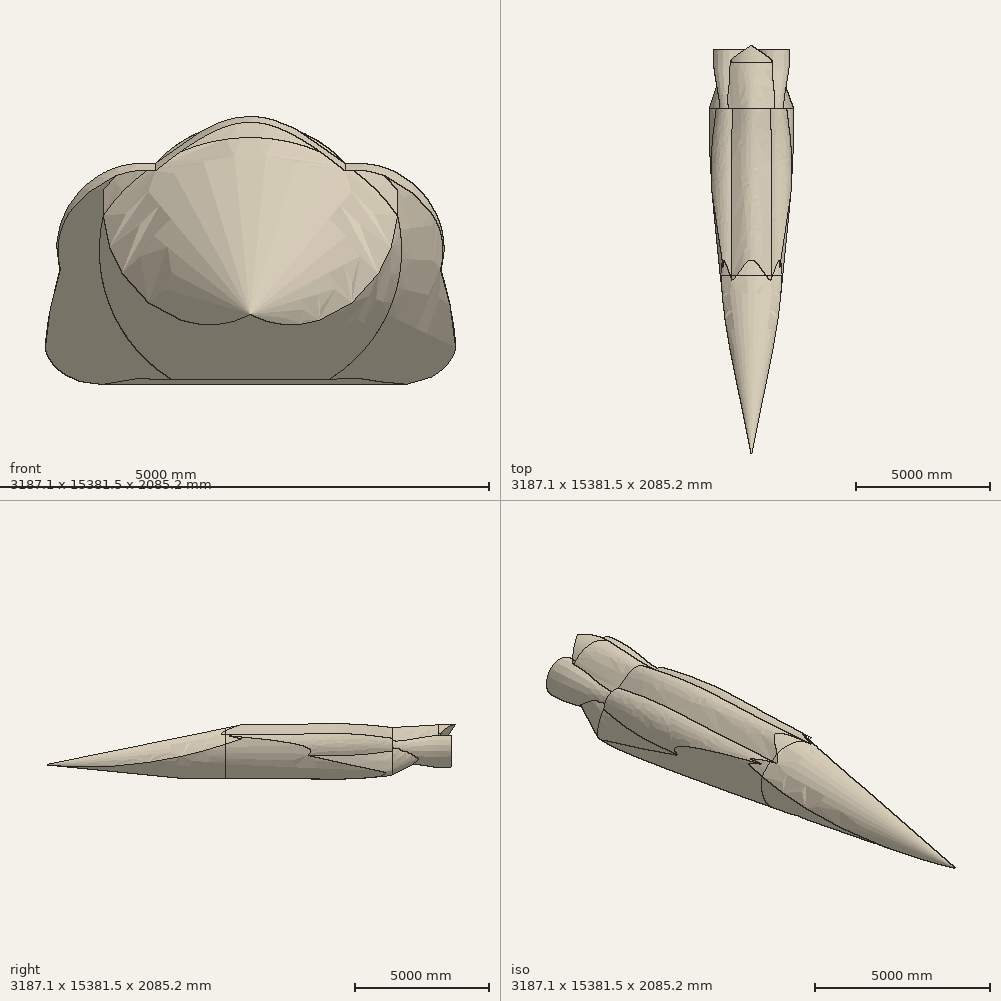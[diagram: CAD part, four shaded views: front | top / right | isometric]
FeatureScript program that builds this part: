
annotation { "Feature Type Name" : "Feature", "Feature Type Description" : "" }
export const myFeature = defineFeature(function(context is Context, id is Id, definition is map)
    precondition{}
    {
        {
            var Q0;
            Q0=qCreatedBy(makeId("Front.planeOp"),FACE);
            cPlane(context, id + "F0", {"entities" : qUnion([Q0]), "cplaneType" : CPlaneType.OFFSET, "offset" : 1750 * mm, "width" : 152.4 * mm, "height" : 152.4 * mm});
        }
        {
            var Q0;
            Q0=qCreatedBy(id+"F0.planeOp",FACE);
            var sketch = newSketch(context, id + "F1", { "sketchPlane" : qUnion([Q0])});
            skLineSegment(sketch, "E0.top", {"start": v(-1394.2, -1000) * mm, "end": v(1394.2, -1000) * mm});
            skPoint(sketch, "E0.middle", {"position": v(0, 0) * mm});
            skFitSpline(sketch, "E1", {"points": [v(-1600, -1000) * mm, v(-848, 530) * mm, v(0, 1000) * mm, v(848, 530) * mm, v(1600, -1000) * mm], "startDerivative": vector(0, 10524.75) * mm, "endDerivative": vector(0, -10524.75) * mm});
            skArc(sketch, "E2", {"start": v(-735.27, 618.52) * mm, "mid": v(-1273.27, 435.52) * mm, "end": v(-1440.68, -107.53) * mm});
            skArc(sketch, "E3.trimOffspring", {"start": v(1440.68, -107.53) * mm, "mid": v(1273.27, 435.52) * mm, "end": v(735.27, 618.52) * mm});
            skFitSpline(sketch, "E4.trimOffspring", {"points": [v(-1600, -1000) * mm, v(-848, 530) * mm, v(0, 1000) * mm, v(848, 530) * mm, v(1600, -1000) * mm], "startDerivative": vector(0, 10524.75) * mm, "endDerivative": vector(0, -10524.75) * mm});
            skFitSpline(sketch, "E5.trimOffspring", {"points": [v(-1600, -1000) * mm, v(-848, 530) * mm, v(0, 1000) * mm, v(848, 530) * mm, v(1600, -1000) * mm], "startDerivative": vector(0, 10524.75) * mm, "endDerivative": vector(0, -10524.75) * mm});
            skArc(sketch, "E6.filletArc", {"start": v(-1593.82, -787.83) * mm, "mid": v(-1539.85, -937.05) * mm, "end": v(-1394.2, -1000) * mm});
            skArc(sketch, "E7.filletArc", {"start": v(1394.2, -1000) * mm, "mid": v(1539.85, -937.05) * mm, "end": v(1593.82, -787.83) * mm});
            skSolve(sketch);
        }
        {
            var Q0;
            Q0=qCreatedBy(makeId("Front.planeOp"),FACE);
            var sketch = newSketch(context, id + "F2", { "sketchPlane" : qUnion([Q0])});
            skLineSegment(sketch, "E8.top", {"start": v(-1394.2, -1000) * mm, "end": v(1394.2, -1000) * mm});
            skPoint(sketch, "E8.middle", {"position": v(0, 0) * mm});
            skFitSpline(sketch, "E9", {"points": [v(-1600, -1000) * mm, v(-848, 530) * mm, v(0, 1000) * mm, v(848, 530) * mm, v(1600, -1000) * mm], "startDerivative": vector(0, 10524.75) * mm, "endDerivative": vector(0, -10524.75) * mm});
            skArc(sketch, "E10", {"start": v(-735.27, 618.52) * mm, "mid": v(-1273.27, 435.52) * mm, "end": v(-1440.68, -107.53) * mm});
            skArc(sketch, "E11.trimOffspring", {"start": v(1440.68, -107.53) * mm, "mid": v(1273.27, 435.52) * mm, "end": v(735.27, 618.52) * mm});
            skFitSpline(sketch, "E12.trimOffspring", {"points": [v(-1600, -1000) * mm, v(-848, 530) * mm, v(0, 1000) * mm, v(848, 530) * mm, v(1600, -1000) * mm], "startDerivative": vector(0, 10524.75) * mm, "endDerivative": vector(0, -10524.75) * mm});
            skFitSpline(sketch, "E13.trimOffspring", {"points": [v(-1600, -1000) * mm, v(-848, 530) * mm, v(0, 1000) * mm, v(848, 530) * mm, v(1600, -1000) * mm], "startDerivative": vector(0, 10524.75) * mm, "endDerivative": vector(0, -10524.75) * mm});
            skArc(sketch, "E14.filletArc", {"start": v(-1593.82, -787.83) * mm, "mid": v(-1539.85, -937.05) * mm, "end": v(-1394.2, -1000) * mm});
            skArc(sketch, "E15.filletArc", {"start": v(1394.2, -1000) * mm, "mid": v(1539.85, -937.05) * mm, "end": v(1593.82, -787.83) * mm});
            skSolve(sketch);
        }
        {
            var Q0;
            Q0=qCreatedBy(makeId("Front.planeOp"),FACE);
            cPlane(context, id + "F3", {"entities" : qUnion([Q0]), "cplaneType" : CPlaneType.OFFSET, "offset" : 3500 * mm, "oppositeDirection" : true, "width" : 150 * mm, "height" : 150 * mm});
        }
        {
            var Q0;
            Q0=qCreatedBy(id+"F3.planeOp",FACE);
            var sketch = newSketch(context, id + "F4", { "sketchPlane" : qUnion([Q0])});
            skLineSegment(sketch, "E16.top", {"start": v(-1394.2, -1000) * mm, "end": v(1394.2, -1000) * mm});
            skPoint(sketch, "E16.middle", {"position": v(0, 0) * mm});
            skFitSpline(sketch, "E17", {"points": [v(-1600, -1000) * mm, v(-848, 530) * mm, v(0, 1000) * mm, v(848, 530) * mm, v(1600, -1000) * mm], "startDerivative": vector(0, 10524.75) * mm, "endDerivative": vector(0, -10524.75) * mm});
            skArc(sketch, "E18", {"start": v(-735.27, 618.52) * mm, "mid": v(-1273.27, 435.52) * mm, "end": v(-1440.68, -107.53) * mm});
            skArc(sketch, "E19.trimOffspring", {"start": v(1440.68, -107.53) * mm, "mid": v(1273.27, 435.52) * mm, "end": v(735.27, 618.52) * mm});
            skFitSpline(sketch, "E20.trimOffspring", {"points": [v(-1600, -1000) * mm, v(-848, 530) * mm, v(0, 1000) * mm, v(848, 530) * mm, v(1600, -1000) * mm], "startDerivative": vector(0, 10524.75) * mm, "endDerivative": vector(0, -10524.75) * mm});
            skFitSpline(sketch, "E21.trimOffspring", {"points": [v(-1600, -1000) * mm, v(-848, 530) * mm, v(0, 1000) * mm, v(848, 530) * mm, v(1600, -1000) * mm], "startDerivative": vector(0, 10524.75) * mm, "endDerivative": vector(0, -10524.75) * mm});
            skArc(sketch, "E22.filletArc", {"start": v(-1593.82, -787.83) * mm, "mid": v(-1539.85, -937.05) * mm, "end": v(-1394.2, -1000) * mm});
            skArc(sketch, "E23.filletArc", {"start": v(1394.2, -1000) * mm, "mid": v(1539.85, -937.05) * mm, "end": v(1593.82, -787.83) * mm});
            skSolve(sketch);
        }
        {
            var Q0;
            Q0=qCreatedBy(makeId("Front.planeOp"),FACE);
            cPlane(context, id + "F5", {"entities" : qUnion([Q0]), "cplaneType" : CPlaneType.OFFSET, "offset" : 4500 * mm, "oppositeDirection" : true, "width" : 150 * mm, "height" : 150 * mm});
        }
        {
            var Q0;
            Q0=qCreatedBy(id+"F5.planeOp",FACE);
            var sketch = newSketch(context, id + "F6", { "sketchPlane" : qUnion([Q0])});
            skLineSegment(sketch, "E24.top", {"start": v(-1413.07, -900) * mm, "end": v(1413.07, -900) * mm});
            skPoint(sketch, "E24.middle", {"position": v(0, 0) * mm});
            skFitSpline(sketch, "E25", {"points": [v(-1600, -900) * mm, v(-784.42, 441.24) * mm, v(0, 900) * mm, v(784.42, 441.24) * mm, v(1600, -900) * mm], "startDerivative": vector(0, 9508.62) * mm, "endDerivative": vector(0, -9508.62) * mm});
            skArc(sketch, "E26", {"start": v(-719.25, 488.69) * mm, "mid": v(-1131.76, 394.84) * mm, "end": v(-1324.66, 18.33) * mm});
            skArc(sketch, "E27.trimOffspring", {"start": v(1324.66, 18.33) * mm, "mid": v(1131.76, 394.84) * mm, "end": v(719.25, 488.69) * mm});
            skFitSpline(sketch, "E28.trimOffspring", {"points": [v(-1600, -900) * mm, v(-784.42, 441.24) * mm, v(0, 900) * mm, v(784.42, 441.24) * mm, v(1600, -900) * mm], "startDerivative": vector(0, 9508.62) * mm, "endDerivative": vector(0, -9508.62) * mm});
            skFitSpline(sketch, "E29.trimOffspring", {"points": [v(-1600, -900) * mm, v(-784.42, 441.24) * mm, v(0, 900) * mm, v(784.42, 441.24) * mm, v(1600, -900) * mm], "startDerivative": vector(0, 9508.62) * mm, "endDerivative": vector(0, -9508.62) * mm});
            skArc(sketch, "E30.filletArc", {"start": v(-1592.48, -705.43) * mm, "mid": v(-1545.4, -842.02) * mm, "end": v(-1413.07, -900) * mm});
            skArc(sketch, "E31.filletArc", {"start": v(1413.07, -900) * mm, "mid": v(1545.4, -842.02) * mm, "end": v(1592.48, -705.43) * mm});
            skLineSegment(sketch, "E32", {"start": v(-719.25, 488.69) * mm, "end": v(-1324.66, 18.33) * mm, "construction": true});
            skLineSegment(sketch, "E33", {"start": v(719.25, 488.69) * mm, "end": v(1324.66, 18.33) * mm, "construction": true});
            skSolve(sketch);
        }
        {
            var Q0;
            Q0=qCreatedBy(makeId("Front.planeOp"),FACE);
            cPlane(context, id + "F7", {"entities" : qUnion([Q0]), "cplaneType" : CPlaneType.OFFSET, "offset" : 6232.05 * mm, "oppositeDirection" : true, "width" : 150 * mm, "height" : 150 * mm});
        }
        {
            var Q0;
            Q0=qCreatedBy(id+"F7.planeOp",FACE);
            var sketch = newSketch(context, id + "F8", { "sketchPlane" : qUnion([Q0])});
            skArc(sketch, "E34", {"start": v(998.61, 52.63) * mm, "mid": v(0, 1000) * mm, "end": v(-998.61, 52.63) * mm});
            skLineSegment(sketch, "E35", {"start": v(0, 0) * mm, "end": v(-948.68, 0) * mm});
            skLineSegment(sketch, "E36", {"start": v(0, 0) * mm, "end": v(948.68, 0) * mm});
            skPoint(sketch, "E37.visualSharp", {"position": v(-1000, 0) * mm});
            skArc(sketch, "E37.filletArc", {"start": v(-998.61, 52.63) * mm, "mid": v(-984.96, 15.59) * mm, "end": v(-948.68, 0) * mm});
            skPoint(sketch, "E38.visualSharp", {"position": v(1000, 0) * mm});
            skArc(sketch, "E38.filletArc", {"start": v(948.68, 0) * mm, "mid": v(984.96, 15.59) * mm, "end": v(998.61, 52.63) * mm});
            skLineSegment(sketch, "E39", {"start": v(0, 1000) * mm, "end": v(0, 675) * mm, "construction": true});
            skPoint(sketch, "E39.endSnap0", {"position": v(0, 1000) * mm});
            skLineSegment(sketch, "E40", {"start": v(0, 675) * mm, "end": v(737.82, 675) * mm, "construction": true});
            skLineSegment(sketch, "E41", {"start": v(0, 675) * mm, "end": v(-737.82, 675) * mm, "construction": true});
            skSolve(sketch);
        }
        {
            var Q0;
            Q0 = qSketchRegion(id + "F1", true);
            var Q1;
            Q1 = qSketchRegion(id + "F2", true);
            var Q2;
            Q2 = qSketchRegion(id + "F4", true);
            var Q3;
            Q3 = qSketchRegion(id + "F6", true);
            loft(context, id + "F9", {"sheetProfilesArray" : [{ "sheetProfileEntities" : qUnion([Q0]) }, { "sheetProfileEntities" : qUnion([Q1]) }, { "sheetProfileEntities" : qUnion([Q2]) }, { "sheetProfileEntities" : qUnion([Q3]) }]});
        }
        {
            var Q0;
            Q0=sQuery(id+"F6.wireOp",EDGE,"E32");
            var Q1;
            Q1=sQuery(id+"F8.wireOp",VERTEX,"E41.end");
            cPlane(context, id + "F10", {"entities" : qUnion([Q0, Q1]), "cplaneType" : CPlaneType.LINE_ANGLE, "offset" : 25 * mm, "angle" : 0 * degree, "width" : 150 * mm, "height" : 150 * mm});
        }
        {
            var Q0;
            Q0=qCreatedBy(id+"F10.planeOp",FACE);
            var sketch = newSketch(context, id + "F11", { "sketchPlane" : qUnion([Q0])});
            skLineSegment(sketch, "E42", {"start": v(-589.34, -4526.34) * mm, "end": v(-612.8, -6268.32) * mm});
            skLineSegment(sketch, "E43", {"start": v(-1354.08, -4472.19) * mm, "end": v(-612.8, -6268.32) * mm});
            skSolve(sketch);
        }
        {
            var Q0;
            Q0=sQuery(id+"F6.wireOp",EDGE,"E33");
            var Q1;
            Q1=sQuery(id+"F8.wireOp",VERTEX,"E40.end");
            cPlane(context, id + "F12", {"entities" : qUnion([Q0, Q1]), "cplaneType" : CPlaneType.LINE_ANGLE, "offset" : 25 * mm, "angle" : 0 * degree, "width" : 150 * mm, "height" : 150 * mm});
        }
        {
            var Q0;
            Q0=qCreatedBy(id+"F12.planeOp",FACE);
            var sketch = newSketch(context, id + "F13", { "sketchPlane" : qUnion([Q0])});
            skLineSegment(sketch, "E44", {"start": v(589.34, 4526.34) * mm, "end": v(612.8, 6268.32) * mm});
            skLineSegment(sketch, "E45", {"start": v(1354.08, 4472.19) * mm, "end": v(612.8, 6268.32) * mm});
            skSolve(sketch);
        }
        {
            var Q1;
            Q1=makeQuery(id+"F6.imprint","IMPRINT",FACE,{"disambiguationData":[TD([[makeQuery(id+"F6.imprint","IMPRINT",EDGE,{"derivedFrom":sQuery(id+"F6.wireOp",EDGE,"E24.top")}),1.0]])]});
            var Q2;
            Q2=makeQuery(id+"F8.imprint","IMPRINT",FACE,{"disambiguationData":[TD([[makeQuery(id+"F8.imprint","IMPRINT",EDGE,{"derivedFrom":sQuery(id+"F8.wireOp",EDGE,"E34")}),1.0]])]});
            var Q3;
            Q3=sQuery(id+"F11.wireOp",EDGE,"E42");
            var Q4;
            Q4=sQuery(id+"F13.wireOp",EDGE,"E44");
            loft(context, id + "F14", {"operationType" : NewBodyOperationType.ADD, "addGuides" : true, "sheetProfilesArray" : [{ "sheetProfileEntities" : qUnion([Q1]) }, { "sheetProfileEntities" : qUnion([Q2]) }], "guidesArray" : [{ "guideEntities" : qUnion([Q3]), "guideDerivativeType" : LoftGuideDerivativeType.DEFAULT, "guideDerivativeMagnitude" : 1 }, { "guideEntities" : qUnion([Q4]), "guideDerivativeType" : LoftGuideDerivativeType.DEFAULT, "guideDerivativeMagnitude" : 1 }]});
        }
        {
            var Q0;
            Q0=makeQuery(id+"F14.opLoft","CAP_FACE",FACE,{"disambiguationData":[OSD([makeQuery(id+"F8.imprint","IMPRINT",FACE,{"disambiguationData":[TD([[makeQuery(id+"F8.imprint","IMPRINT",EDGE,{"derivedFrom":sQuery(id+"F8.wireOp",EDGE,"E34")}),1.0]])]})])],"isStart":true});
            extrude(context, id + "F15", {"entities" : qUnion([Q0]), "operationType" : NewBodyOperationType.ADD, "depth" : 649.4 * mm});
        }
        {
            var Q0;
            Q0=qCreatedBy(makeId("Right.planeOp"),FACE);
            var sketch = newSketch(context, id + "F16", { "sketchPlane" : qUnion([Q0])});
            skLineSegment(sketch, "E46", {"start": v(0, 0) * mm, "end": v(4500, 0) * mm});
            skLineSegment(sketch, "E47", {"start": v(4500, 0) * mm, "end": v(6232.05, 0) * mm});
            skLineSegment(sketch, "E48", {"start": v(4500, 0) * mm, "end": v(4500, 1000) * mm});
            skLineSegment(sketch, "E49", {"start": v(4500, 1000) * mm, "end": v(6881.46, 1000) * mm});
            skLineSegment(sketch, "E50", {"start": v(6881.46, 1000) * mm, "end": v(6881.46, -1000) * mm});
            skLineSegment(sketch, "E51", {"start": v(6881.46, 1000) * mm, "end": v(6232.05, 0) * mm});
            skLineSegment(sketch, "E52", {"start": v(6232.05, 0) * mm, "end": v(5582.64, -1000) * mm});
            skLineSegment(sketch, "E53", {"start": v(5582.64, -1000) * mm, "end": v(6881.46, -1000) * mm});
            skSolve(sketch);
        }
        {
            var Q0;
            Q0=makeQuery(id+"F16.imprint","IMPRINT",FACE,{"disambiguationData":[TD([[makeQuery(id+"F16.imprint","IMPRINT",EDGE,{"derivedFrom":sQuery(id+"F16.wireOp",EDGE,"E50")}),-1.0]])]});
            var Q1;
            Q1=sQuery(id+"F16.wireOp",EDGE,"E49");
            revolve(context, id + "F17", {"operationType" : NewBodyOperationType.REMOVE, "entities" : qUnion([Q0]), "axis" : qUnion([Q1]), "revolveType" : RevolveType.SYMMETRIC, "oppositeDirection" : true, "angle" : 182 * degree});
        }
        {
            var Q0;
            Q0=makeQuery(id+"F9.opLoft","CAP_FACE",FACE,{"disambiguationData":[OSD([makeQuery(id+"F1.imprint","IMPRINT",FACE,{"disambiguationData":[TD([[makeQuery(id+"F1.imprint","IMPRINT",EDGE,{"derivedFrom":sQuery(id+"F1.wireOp",EDGE,"E0.top")}),1.0]])]})])],"isStart":true});
            extrude(context, id + "F18", {"entities" : qUnion([Q0]), "depth" : 6750 * mm});
        }
        {
            var Q0;
            Q0=qCreatedBy(makeId("Right.planeOp"),FACE);
            var sketch = newSketch(context, id + "F19", { "sketchPlane" : qUnion([Q0])});
            skLineSegment(sketch, "E54", {"start": v(0, 0) * mm, "end": v(-3500, 0) * mm});
            skLineSegment(sketch, "E55", {"start": v(-3500, 0) * mm, "end": v(-3500, -1000) * mm});
            skLineSegment(sketch, "E56", {"start": v(-3500, -1000) * mm, "end": v(-8500, -1000) * mm});
            skLineSegment(sketch, "E57", {"start": v(-8500, -1000) * mm, "end": v(-8500, -499.31) * mm});
            skLineSegment(sketch, "E58", {"start": v(-1151.4, 0) * mm, "end": v(-1151.4, 1000) * mm});
            skLineSegment(sketch, "E59", {"start": v(-1151.4, 1000) * mm, "end": v(-8500, -499.31) * mm});
            skLineSegment(sketch, "E60", {"start": v(-8500, -499.31) * mm, "end": v(-3500, -1000) * mm});
            skLineSegment(sketch, "E61", {"start": v(-1151.4, 1000) * mm, "end": v(-8500, 1000) * mm});
            skLineSegment(sketch, "E62", {"start": v(-8500, 1000) * mm, "end": v(-8500, -499.31) * mm});
            skLineSegment(sketch, "E63", {"start": v(-8500, -1000) * mm, "end": v(-8500, -1980) * mm});
            skLineSegment(sketch, "E64", {"start": v(-3500, -1000) * mm, "end": v(6286.5, -1980) * mm});
            skLineSegment(sketch, "E65", {"start": v(6286.5, -1980) * mm, "end": v(-8500, -1980) * mm});
            skLineSegment(sketch, "E66", {"start": v(-8500, -499.31) * mm, "end": v(-3500, -499.31) * mm});
            skSolve(sketch);
        }
        {
            var Q0;
            Q0=makeQuery(id+"F19.imprint","IMPRINT",FACE,{"disambiguationData":[TD([[makeQuery(id+"F19.imprint","IMPRINT",EDGE,{"derivedFrom":sQuery(id+"F19.wireOp",EDGE,"E59")}),-1.0]])]});
            var Q1;
            Q1=sQuery(id+"F19.wireOp",EDGE,"E66");
            revolve(context, id + "F20", {"operationType" : NewBodyOperationType.REMOVE, "entities" : qUnion([Q0]), "axis" : qUnion([Q1]), "revolveType" : RevolveType.SYMMETRIC, "oppositeDirection" : true, "angle" : 250 * degree});
        }
        {
            var Q0;
            Q0=makeQuery(id+"F19.imprint","IMPRINT",FACE,{"disambiguationData":[TD([[makeQuery(id+"F19.imprint","IMPRINT",EDGE,{"derivedFrom":sQuery(id+"F19.wireOp",EDGE,"E56")}),-1.0]])]});
            var Q1;
            Q1=makeQuery(id+"F19.imprint","IMPRINT",FACE,{"disambiguationData":[TD([[makeQuery(id+"F19.imprint","IMPRINT",EDGE,{"derivedFrom":sQuery(id+"F19.wireOp",EDGE,"E56")}),1.0]])]});
            var Q2;
            Q2=sQuery(id+"F19.wireOp",EDGE,"E54");
            revolve(context, id + "F21", {"operationType" : NewBodyOperationType.REMOVE, "entities" : qUnion([Q0, Q1]), "axis" : qUnion([Q2]), "revolveType" : RevolveType.SYMMETRIC, "oppositeDirection" : true, "angle" : 240 * degree});
        }
        {
            var Q0;
            Q0=qCreatedBy(makeId("Front.planeOp"),FACE);
            cPlane(context, id + "F22", {"entities" : qUnion([Q0]), "cplaneType" : CPlaneType.OFFSET, "offset" : 3500 * mm, "oppositeDirection" : true, "width" : 150 * mm, "height" : 150 * mm});
        }
        {
            var Q0;
            Q0=qCreatedBy(id+"F22.planeOp",FACE);
            var sketch = newSketch(context, id + "F23", { "sketchPlane" : qUnion([Q0])});
            skCircle(sketch, "E67", {"center": v(-825, 0) * mm, "radius": 600 * mm});
            skCircle(sketch, "E68", {"center": v(825, 0) * mm, "radius": 600 * mm});
            skSolve(sketch);
        }
        {
            var Q0;
            Q0=qCreatedBy(makeId("Front.planeOp"),FACE);
            cPlane(context, id + "F24", {"entities" : qUnion([Q0]), "cplaneType" : CPlaneType.OFFSET, "offset" : 4500 * mm, "oppositeDirection" : true, "width" : 150 * mm, "height" : 150 * mm});
        }
        {
            var Q0;
            Q0=qCreatedBy(id+"F24.planeOp",FACE);
            var sketch = newSketch(context, id + "F25", { "sketchPlane" : qUnion([Q0])});
            skCircle(sketch, "E69", {"center": v(-825, 0) * mm, "radius": 400 * mm});
            skCircle(sketch, "E70", {"center": v(825, 0) * mm, "radius": 400 * mm});
            skSolve(sketch);
        }
        {
            var Q0;
            Q0=qCreatedBy(makeId("Front.planeOp"),FACE);
            cPlane(context, id + "F26", {"entities" : qUnion([Q0]), "cplaneType" : CPlaneType.OFFSET, "offset" : 6232.05 * mm, "oppositeDirection" : true, "width" : 150 * mm, "height" : 150 * mm});
        }
        {
            var Q0;
            Q0=qCreatedBy(id+"F26.planeOp",FACE);
            var sketch = newSketch(context, id + "F27", { "sketchPlane" : qUnion([Q0])});
            skCircle(sketch, "E71", {"center": v(-825, 0) * mm, "radius": 600 * mm});
            skCircle(sketch, "E72", {"center": v(825, 0) * mm, "radius": 600 * mm});
            skSolve(sketch);
        }
        {
            var Q0;
            Q0=qCreatedBy(makeId("Front.planeOp"),FACE);
            cPlane(context, id + "F28", {"entities" : qUnion([Q0]), "cplaneType" : CPlaneType.OFFSET, "offset" : 6732.05 * mm, "oppositeDirection" : true, "width" : 150 * mm, "height" : 150 * mm});
        }
        {
            var Q0;
            Q0=qCreatedBy(id+"F28.planeOp",FACE);
            var sketch = newSketch(context, id + "F29", { "sketchPlane" : qUnion([Q0])});
            skCircle(sketch, "E73", {"center": v(-825, 0) * mm, "radius": 600 * mm});
            skCircle(sketch, "E74", {"center": v(825, 0) * mm, "radius": 600 * mm});
            skSolve(sketch);
        }
        {
            var Q0;
            Q0=makeQuery(id+"F23.imprint","IMPRINT",FACE,{"disambiguationData":[TD([[makeQuery(id+"F23.imprint","IMPRINT",EDGE,{"derivedFrom":sQuery(id+"F23.wireOp",EDGE,"E67")}),1.0]])]});
            var Q1;
            Q1=makeQuery(id+"F25.imprint","IMPRINT",FACE,{"disambiguationData":[TD([[makeQuery(id+"F25.imprint","IMPRINT",EDGE,{"derivedFrom":sQuery(id+"F25.wireOp",EDGE,"E69")}),1.0]])]});
            var Q2;
            Q2=makeQuery(id+"F27.imprint","IMPRINT",FACE,{"disambiguationData":[TD([[makeQuery(id+"F27.imprint","IMPRINT",EDGE,{"derivedFrom":sQuery(id+"F27.wireOp",EDGE,"E71")}),1.0]])]});
            var Q3;
            Q3=makeQuery(id+"F29.imprint","IMPRINT",FACE,{"disambiguationData":[TD([[makeQuery(id+"F29.imprint","IMPRINT",EDGE,{"derivedFrom":sQuery(id+"F29.wireOp",EDGE,"E73")}),1.0]])]});
            loft(context, id + "F30", {"sheetProfilesArray" : [{ "sheetProfileEntities" : qUnion([Q0]) }, { "sheetProfileEntities" : qUnion([Q1]) }, { "sheetProfileEntities" : qUnion([Q2]) }, { "sheetProfileEntities" : qUnion([Q3]) }]});
        }
        {
            var Q0;
            Q0=makeQuery(id+"F23.imprint","IMPRINT",FACE,{"disambiguationData":[TD([[makeQuery(id+"F23.imprint","IMPRINT",EDGE,{"derivedFrom":sQuery(id+"F23.wireOp",EDGE,"E68")}),1.0]])]});
            var Q1;
            Q1=makeQuery(id+"F25.imprint","IMPRINT",FACE,{"disambiguationData":[TD([[makeQuery(id+"F25.imprint","IMPRINT",EDGE,{"derivedFrom":sQuery(id+"F25.wireOp",EDGE,"E70")}),1.0]])]});
            var Q2;
            Q2=makeQuery(id+"F27.imprint","IMPRINT",FACE,{"disambiguationData":[TD([[makeQuery(id+"F27.imprint","IMPRINT",EDGE,{"derivedFrom":sQuery(id+"F27.wireOp",EDGE,"E72")}),1.0]])]});
            var Q3;
            Q3=makeQuery(id+"F29.imprint","IMPRINT",FACE,{"disambiguationData":[TD([[makeQuery(id+"F29.imprint","IMPRINT",EDGE,{"derivedFrom":sQuery(id+"F29.wireOp",EDGE,"E74")}),1.0]])]});
            loft(context, id + "F31", {"sheetProfilesArray" : [{ "sheetProfileEntities" : qUnion([Q0]) }, { "sheetProfileEntities" : qUnion([Q1]) }, { "sheetProfileEntities" : qUnion([Q2]) }, { "sheetProfileEntities" : qUnion([Q3]) }]});
        }
    });
